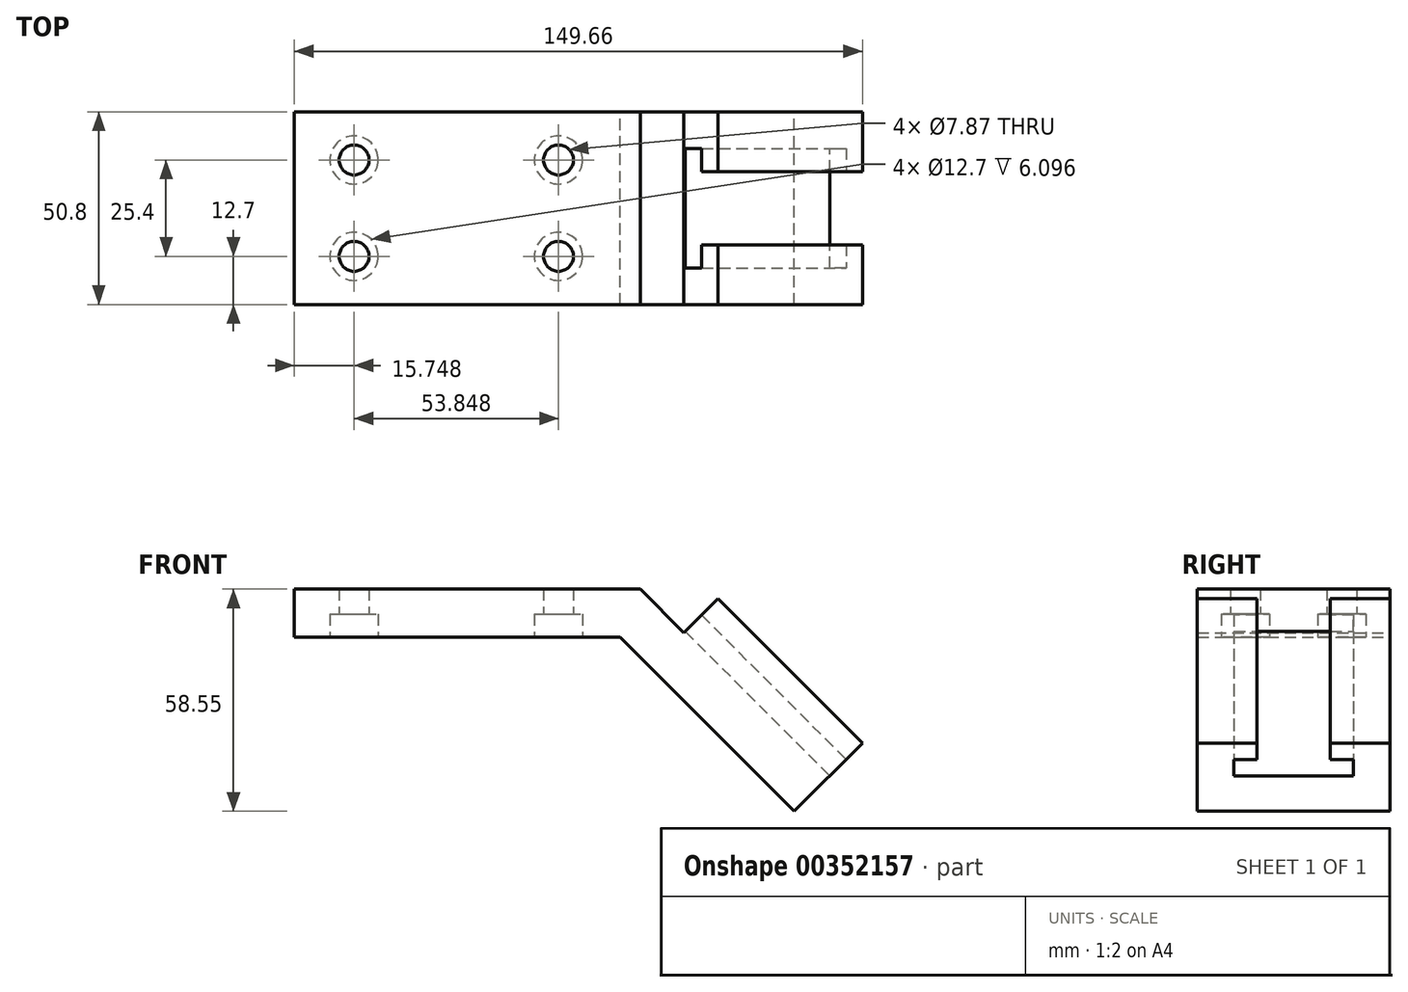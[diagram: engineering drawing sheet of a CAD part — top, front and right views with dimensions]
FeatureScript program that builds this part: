
annotation { "Feature Type Name" : "Feature", "Feature Type Description" : "" }
export const myFeature = defineFeature(function(context is Context, id is Id, definition is map)
    precondition{}
    {
        {
            var Q0;
            Q0=qCreatedBy(makeId("Front.planeOp"),FACE);
            var sketch = newSketch(context, id + "F0", { "sketchPlane" : qUnion([Q0])});
            skLineSegment(sketch, "E0", {"start": v(0, 0) * mm, "end": v(0, 12.7) * mm});
            skLineSegment(sketch, "E1", {"start": v(0, 12.7) * mm, "end": v(0, 0) * mm});
            skLineSegment(sketch, "E2", {"start": v(0, 0) * mm, "end": v(85.85, 0) * mm});
            skLineSegment(sketch, "E3", {"start": v(85.85, 0) * mm, "end": v(131.7, -45.85) * mm});
            skLineSegment(sketch, "E4", {"start": v(131.7, -45.85) * mm, "end": v(149.66, -27.9) * mm});
            skLineSegment(sketch, "E5", {"start": v(149.66, -27.9) * mm, "end": v(111.59, 10.19) * mm});
            skLineSegment(sketch, "E6", {"start": v(111.59, 10.19) * mm, "end": v(102.6, 1.2) * mm});
            skLineSegment(sketch, "E7", {"start": v(102.6, 1.2) * mm, "end": v(91.11, 12.7) * mm});
            skLineSegment(sketch, "E8", {"start": v(0, 12.7) * mm, "end": v(91.11, 12.7) * mm});
            skLineSegment(sketch, "E9", {"start": v(91.11, 12.7) * mm, "end": v(140.68, -36.87) * mm, "construction": true});
            skSolve(sketch);
        }
        {
            var Q0;
            Q0 = qSketchRegion(id + "F0", true);
            extrude(context, id + "F1", {"entities" : qUnion([Q0]), "depth" : 50.8 * mm});
        }
        {
            var Q0;
            Q0=makeQuery(id+"F1.opExtrude","SWEPT_FACE",FACE,{"disambiguationData":[OSD([sQuery(id+"F0.wireOp",EDGE,"E2")])]});
            var sketch = newSketch(context, id + "F2", { "sketchPlane" : qUnion([Q0])});
            skPoint(sketch, "E10", {"position": v(15.75, 38.1) * mm});
            skPoint(sketch, "E11", {"position": v(15.75, 12.7) * mm});
            skPoint(sketch, "E12", {"position": v(69.6, 12.7) * mm});
            skPoint(sketch, "E13", {"position": v(69.6, 38.1) * mm});
            skSolve(sketch);
        }
        {
            var Q0;
            Q0=sQuery(id+"F2.wireOp",VERTEX,"E10");
            var Q1;
            Q1=sQuery(id+"F2.wireOp",VERTEX,"E13");
            var Q2;
            Q2=sQuery(id+"F2.wireOp",VERTEX,"E12");
            var Q3;
            Q3=sQuery(id+"F2.wireOp",VERTEX,"E11");
            var Q4;
            Q4=makeQuery(id+"F1.opExtrude","SWEPT_BODY",BODY,{"disambiguationData":[OSD([sQuery(id+"F0.wireOp",EDGE,"E1"),sQuery(id+"F0.wireOp",EDGE,"E2"),sQuery(id+"F0.wireOp",EDGE,"E3"),sQuery(id+"F0.wireOp",EDGE,"E4"),sQuery(id+"F0.wireOp",EDGE,"E5"),sQuery(id+"F0.wireOp",EDGE,"E6"),sQuery(id+"F0.wireOp",EDGE,"E7"),sQuery(id+"F0.wireOp",EDGE,"E8")])]});
            hole(context, id + "F3", {"style" : HoleStyle.C_BORE, "endStyle" : HoleEndStyle.THROUGH, "holeDiameter" : 7.87 * mm, "cBoreDiameter" : 12.7 * mm, "cBoreDepth" : 6.1 * mm, "isTappedThrough" : true, "tappedDepth" : 12.7 * mm, "tapClearance" : 3, "locations" : qUnion([Q0, Q1, Q2, Q3]), "scope" : qUnion([Q4])});
        }
        {
            var Q0;
            Q0=makeQuery(id+"F1.opExtrude","SWEPT_FACE",FACE,{"disambiguationData":[OSD([sQuery(id+"F0.wireOp",EDGE,"E5")])]});
            var sketch = newSketch(context, id + "F4", { "sketchPlane" : qUnion([Q0])});
            skSolve(sketch);
        }
        {
            var Q0;
            Q0=makeQuery(id+"F1.opExtrude","SWEPT_FACE",FACE,{"disambiguationData":[OSD([sQuery(id+"F0.wireOp",EDGE,"E4")])]});
            var sketch = newSketch(context, id + "F5", { "sketchPlane" : qUnion([Q0])});
            skLineSegment(sketch, "E14", {"start": v(-50.8, 86.1) * mm, "end": v(0, 86.1) * mm});
            skLineSegment(sketch, "E15", {"start": v(-35.05, 86.1) * mm, "end": v(-35.05, 80.01) * mm});
            skLineSegment(sketch, "E16", {"start": v(-15.75, 86.1) * mm, "end": v(-15.75, 80.01) * mm});
            skLineSegment(sketch, "E17", {"start": v(-35.05, 80.01) * mm, "end": v(-41.15, 80.01) * mm});
            skLineSegment(sketch, "E18", {"start": v(-41.15, 80.01) * mm, "end": v(-41.15, 73.91) * mm});
            skLineSegment(sketch, "E19", {"start": v(-41.15, 73.91) * mm, "end": v(-9.65, 73.91) * mm});
            skLineSegment(sketch, "E20", {"start": v(-9.65, 73.91) * mm, "end": v(-9.65, 80.01) * mm});
            skLineSegment(sketch, "E21", {"start": v(-9.65, 80.01) * mm, "end": v(-15.75, 80.01) * mm});
            skSolve(sketch);
        }
        {
            var Q0;
            Q0 = qSketchRegion(id + "F5", true);
            extrude(context, id + "F6", {"entities" : qUnion([Q0]), "operationType" : NewBodyOperationType.REMOVE, "endBound" : BoundingType.THROUGH_ALL, "oppositeDirection" : true, "depth" : 25.4 * mm});
        }
        {
            var Q0;
            Q0=makeQuery(id+"F1.opExtrude","SWEPT_FACE",FACE,{"disambiguationData":[OSD([sQuery(id+"F0.wireOp",EDGE,"E3")])]});
            var sketch = newSketch(context, id + "F7", { "sketchPlane" : qUnion([Q0])});
            skArc(sketch, "E22", {"start": v(119.18, 0) * mm, "mid": v(125.55, 25.4) * mm, "end": v(119.18, 50.8) * mm});
            skLineSegment(sketch, "E23", {"start": v(119.18, 50.8) * mm, "end": v(125.55, 50.8) * mm});
            skLineSegment(sketch, "E24", {"start": v(125.55, 50.8) * mm, "end": v(125.55, 0) * mm});
            skLineSegment(sketch, "E25", {"start": v(125.55, 0) * mm, "end": v(119.18, 0) * mm});
            skSolve(sketch);
        }
        {
            var Q0;
            Q0 = qSketchRegion(id + "F7", true);
            extrude(context, id + "F8", {"entities" : qUnion([Q0]), "operationType" : NewBodyOperationType.REMOVE, "endBound" : BoundingType.THROUGH_ALL, "oppositeDirection" : true, "depth" : 25.4 * mm});
        }
    });
